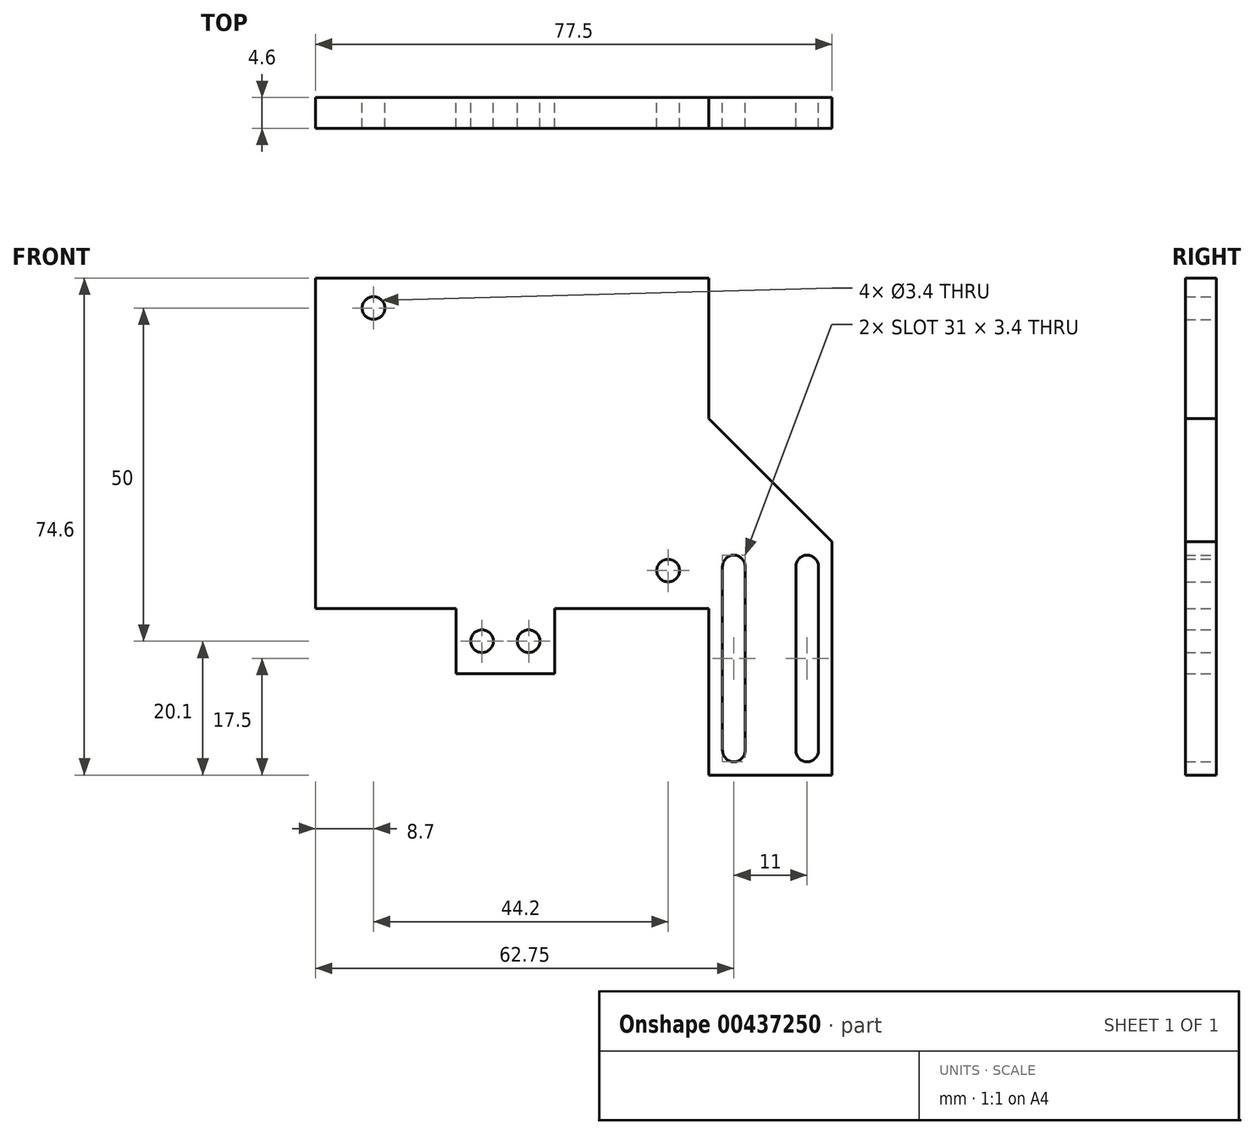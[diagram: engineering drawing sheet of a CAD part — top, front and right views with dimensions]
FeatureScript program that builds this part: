
annotation { "Feature Type Name" : "Feature", "Feature Type Description" : "" }
export const myFeature = defineFeature(function(context is Context, id is Id, definition is map)
    precondition{}
    {
        {
            var Q0;
            Q0=qCreatedBy(makeId("Front.planeOp"),FACE);
            var sketch = newSketch(context, id + "F0", { "sketchPlane" : qUnion([Q0])});
            skLineSegment(sketch, "E0.bottom", {"start": v(-59, 49.6) * mm, "end": v(0, 49.6) * mm});
            skLineSegment(sketch, "E0.top", {"start": v(-59, 0) * mm, "end": v(-37.9, 0) * mm});
            skLineSegment(sketch, "E0.left", {"start": v(-59, 49.6) * mm, "end": v(-59, 0) * mm});
            skLineSegment(sketch, "E0.right", {"start": v(0, 49.6) * mm, "end": v(0, 28.5) * mm});
            skLineSegment(sketch, "E1", {"start": v(-37.9, 0) * mm, "end": v(-37.9, -9.8) * mm});
            skLineSegment(sketch, "E2", {"start": v(-37.9, -9.8) * mm, "end": v(-23.15, -9.8) * mm});
            skLineSegment(sketch, "E3", {"start": v(-23.15, -9.8) * mm, "end": v(-23.15, 0) * mm});
            skLineSegment(sketch, "E4.trimOffspring", {"start": v(-23.15, 0) * mm, "end": v(0, 0) * mm});
            skCircle(sketch, "E5", {"center": v(-50.3, 45.1) * mm, "radius": 1.7 * mm});
            skCircle(sketch, "E6", {"center": v(-6.1, 5.7) * mm, "radius": 1.7 * mm});
            skCircle(sketch, "E7", {"center": v(-34.03, -4.9) * mm, "radius": 1.7 * mm});
            skCircle(sketch, "E8", {"center": v(-27.03, -4.9) * mm, "radius": 1.7 * mm});
            skLineSegment(sketch, "E9", {"start": v(-34.03, -4.9) * mm, "end": v(-27.03, -4.9) * mm, "construction": true});
            skPoint(sketch, "E10", {"position": v(-30.53, -4.9) * mm});
            skLineSegment(sketch, "E11", {"start": v(-37.9, 0) * mm, "end": v(-23.15, 0) * mm, "construction": true});
            skPoint(sketch, "E12", {"position": v(-30.53, 0) * mm});
            skLineSegment(sketch, "E13.trimOffspring", {"start": v(-30.53, 0) * mm, "end": v(-30.53, -9.8) * mm, "construction": true});
            skLineSegment(sketch, "E14.bottom", {"start": v(0, 28.5) * mm, "end": v(18.5, 10) * mm});
            skLineSegment(sketch, "E14.top", {"start": v(0, -25) * mm, "end": v(18.5, -25) * mm});
            skLineSegment(sketch, "E14.left", {"start": v(0, 0) * mm, "end": v(0, -25) * mm});
            skLineSegment(sketch, "E14.right", {"start": v(18.5, 10) * mm, "end": v(18.5, -25) * mm});
            skLineSegment(sketch, "E15.left", {"start": v(2.05, 6.3) * mm, "end": v(2.05, -21.3) * mm});
            skLineSegment(sketch, "E15.right", {"start": v(5.45, 6.3) * mm, "end": v(5.45, -21.3) * mm});
            skLineSegment(sketch, "E16", {"start": v(9.25, -25) * mm, "end": v(9.25, 0) * mm, "construction": true});
            skArc(sketch, "E17", {"start": v(5.45, 6.3) * mm, "mid": v(3.75, 8) * mm, "end": v(2.05, 6.3) * mm});
            skArc(sketch, "E18", {"start": v(2.05, -21.3) * mm, "mid": v(3.75, -23) * mm, "end": v(5.45, -21.3) * mm});
            skLineSegment(sketch, "E19", {"start": v(18.5, 10) * mm, "end": v(0, 10) * mm, "construction": true});
            skArc(sketch, "E20.MirrorCS", {"start": v(16.45, -21.3) * mm, "mid": v(14.75, -23) * mm, "end": v(13.05, -21.3) * mm});
            skArc(sketch, "E21.MirrorCS", {"start": v(13.05, 6.3) * mm, "mid": v(14.75, 8) * mm, "end": v(16.45, 6.3) * mm});
            skLineSegment(sketch, "E22.MirrorCS", {"start": v(16.45, 6.3) * mm, "end": v(16.45, -21.3) * mm});
            skLineSegment(sketch, "E23.MirrorCS", {"start": v(13.05, 6.3) * mm, "end": v(13.05, -21.3) * mm});
            skLineSegment(sketch, "E24", {"start": v(0, 28.5) * mm, "end": v(0, 0) * mm, "construction": true});
            skSolve(sketch);
        }
        {
            var Q0;
            Q0 = qSketchRegion(id + "F0", true);
            extrude(context, id + "F1", {"entities" : qUnion([Q0]), "depth" : 4.6 * mm});
        }
    });
